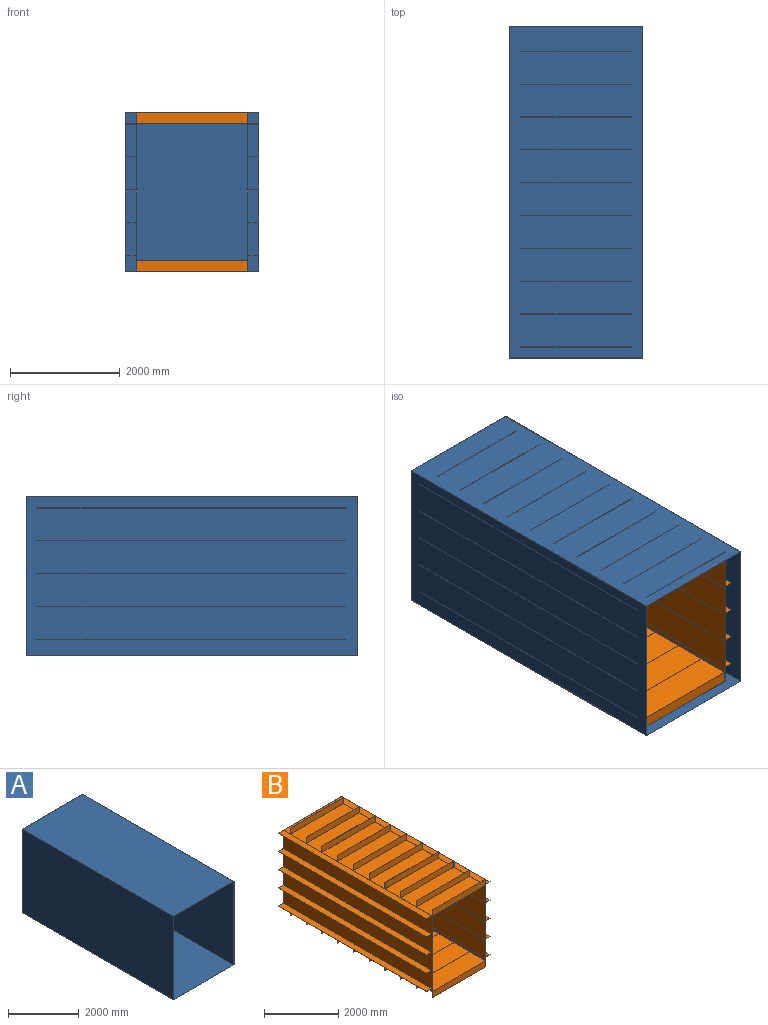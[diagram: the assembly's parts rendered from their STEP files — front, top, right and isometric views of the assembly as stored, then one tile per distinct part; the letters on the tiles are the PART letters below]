
ASSEMBLY  parts=2 mates=1
PART A: 11 faces, bbox 2438x6058x2896 mm
  f0: plane 6058x2438mm, normal (0,0,1), area 14769404mm2, adj f1,f7,f8,f9
  f1: plane 6058x2896mm, normal (-1,0,0), area 17543968mm2, adj f0,f2,f8,f9
  f2: plane 6058x2438mm, normal (0,0,-1), area 14769404mm2, adj f1,f7,f8,f9
  f3: plane 6055x2890mm, normal (1,0,0), area 17498950mm2, adj f4,f6,f8,f10
  f4: plane 6055x2432mm, normal (0,0,-1), area 14725760mm2, adj f3,f5,f8,f10
  f5: plane 6055x2890mm, normal (-1,0,0), area 17498950mm2, adj f4,f6,f8,f10
  f6: plane 6055x2432mm, normal (0,0,1), area 14725760mm2, adj f3,f5,f8,f10
  f7: plane 6058x2896mm, normal (1,0,0), area 17543968mm2, adj f0,f2,f8,f9
  f8: plane 2896x2438mm, normal (0,-1,0), area 31968mm2, adj f0,f1,f2,f3,f4,f5,f6,f7
  f9: plane 2896x2438mm, normal (0,1,0), area 7060448mm2, adj f0,f1,f2,f7
  f10: plane 2890x2432mm, normal (0,-1,0), area 7028480mm2, adj f3,f4,f5,f6
PART B: 135 faces, bbox 2432x5668x2890 mm
  f0: plane 5668x2032mm, normal (0,0,-1), area 11416076mm2, adj f2,f7,f8,f9,f97,f98,f99,f100
  f1: plane 5668x2432mm, normal (0,0,1), area 13671276mm2, adj f2,f7,f8,f9,f11,f12,f29,f31
  f2: plane 5668x2490mm, normal (-1,0,0), area 13972370mm2, adj f0,f1,f8,f9,f30,f31,f32,f34
  f3: plane 5668x2484mm, normal (1,0,0), area 14079312mm2, adj f4,f6,f8,f9
  f4: plane 5668x2026mm, normal (0,0,-1), area 11483368mm2, adj f3,f5,f8,f9
  f5: plane 5668x2484mm, normal (-1,0,0), area 14079312mm2, adj f4,f6,f8,f9
  f6: plane 5668x2026mm, normal (0,0,1), area 11483368mm2, adj f3,f5,f8,f9
  f7: plane 5668x2890mm, normal (1,0,0), area 13983370mm2, adj f0,f1,f8,f9,f10,f12,f13,f14
  f8: plane 2890x2032mm, normal (0,-1,0), area 837496mm2, adj f0,f1,f2,f3,f4,f5,f6,f7
  f9: plane 2490x2432mm, normal (0,1,0), area 37096mm2, adj f0,f1,f2,f3,f4,f5,f6,f7
  f10: plane 5638x200mm, normal (0,0,-1), area 1127600mm2, adj f7,f9,f11,f12
  f11: plane 5638x5mm, normal (1,0,0), area 28190mm2, adj f1,f9,f10,f12
  f12: plane 200x5mm, normal (0,-1,0), area 1000mm2, adj f1,f7,f10,f11
  f13: plane 5638x200mm, normal (0,0,1), area 1127600mm2, adj f7,f9,f15,f16
  f14: plane 5638x200mm, normal (0,0,-1), area 1127600mm2, adj f7,f9,f15,f16
  f15: plane 5638x5mm, normal (1,0,0), area 28190mm2, adj f9,f13,f14,f16
  f16: plane 200x5mm, normal (0,-1,0), area 1000mm2, adj f7,f13,f14,f15
  f17: plane 5638x200mm, normal (0,0,1), area 1127600mm2, adj f7,f9,f19,f20
  f18: plane 5638x200mm, normal (0,0,-1), area 1127600mm2, adj f7,f9,f19,f20
  f19: plane 5638x5mm, normal (1,0,0), area 28190mm2, adj f9,f17,f18,f20
  f20: plane 200x5mm, normal (0,-1,0), area 1000mm2, adj f7,f17,f18,f19
  f21: plane 5638x200mm, normal (0,0,1), area 1127600mm2, adj f7,f9,f23,f24
  f22: plane 5638x200mm, normal (0,0,-1), area 1127600mm2, adj f7,f9,f23,f24
  f23: plane 5638x5mm, normal (1,0,0), area 28190mm2, adj f9,f21,f22,f24
  f24: plane 200x5mm, normal (0,-1,0), area 1000mm2, adj f7,f21,f22,f23
  f25: plane 5638x200mm, normal (0,0,1), area 1127600mm2, adj f7,f9,f27,f28
  f26: plane 5638x200mm, normal (0,0,-1), area 1127600mm2, adj f7,f9,f27,f28
  f27: plane 5638x5mm, normal (1,0,0), area 28190mm2, adj f9,f25,f26,f28
  f28: plane 200x5mm, normal (0,-1,0), area 1000mm2, adj f7,f25,f26,f27
  f29: plane 5638x5mm, normal (-1,0,0), area 28190mm2, adj f1,f9,f30,f31
  f30: plane 5638x200mm, normal (0,0,-1), area 1127600mm2, adj f2,f9,f29,f31
  f31: plane 200x5mm, normal (0,-1,0), area 1000mm2, adj f1,f2,f29,f30
  f32: plane 5638x200mm, normal (0,0,1), area 1127600mm2, adj f2,f9,f33,f35
  f33: plane 5638x5mm, normal (-1,0,0), area 28190mm2, adj f9,f32,f34,f35
  f34: plane 5638x200mm, normal (0,0,-1), area 1127600mm2, adj f2,f9,f33,f35
  f35: plane 200x5mm, normal (0,-1,0), area 1000mm2, adj f2,f32,f33,f34
  f36: plane 5638x200mm, normal (0,0,1), area 1127600mm2, adj f2,f9,f37,f39
  f37: plane 5638x5mm, normal (-1,0,0), area 28190mm2, adj f9,f36,f38,f39
  f38: plane 5638x200mm, normal (0,0,-1), area 1127600mm2, adj f2,f9,f37,f39
  f39: plane 200x5mm, normal (0,-1,0), area 1000mm2, adj f2,f36,f37,f38
  f40: plane 5638x200mm, normal (0,0,1), area 1127600mm2, adj f2,f9,f41,f43
  f41: plane 5638x5mm, normal (-1,0,0), area 28190mm2, adj f9,f40,f42,f43
  f42: plane 5638x200mm, normal (0,0,-1), area 1127600mm2, adj f2,f9,f41,f43
  f43: plane 200x5mm, normal (0,-1,0), area 1000mm2, adj f2,f40,f41,f42
  f44: plane 5638x200mm, normal (0,0,1), area 1127600mm2, adj f2,f9,f45,f47
  f45: plane 5638x5mm, normal (-1,0,0), area 28190mm2, adj f9,f44,f46,f47
  f46: plane 5638x200mm, normal (0,0,-1), area 1127600mm2, adj f2,f9,f45,f47
  f47: plane 200x5mm, normal (0,-1,0), area 1000mm2, adj f2,f44,f45,f46
  f48: plane 2026x200mm, normal (0,1,0), area 405200mm2, adj f1,f7,f49,f50
  f49: plane 2026x5mm, normal (0,0,1), area 10130mm2, adj f7,f8,f48,f50
  f50: plane 200x5mm, normal (-1,0,0), area 1000mm2, adj f1,f8,f48,f49
  f51: plane 2026x200mm, normal (0,-1,0), area 405200mm2, adj f1,f53,f54,f55
  f52: plane 2026x200mm, normal (0,1,0), area 405200mm2, adj f1,f53,f54,f55
  f53: plane 2026x5mm, normal (0,0,1), area 10130mm2, adj f51,f52,f54,f55
  f54: plane 200x5mm, normal (-1,0,0), area 1000mm2, adj f1,f51,f52,f53
  f55: plane 200x5mm, normal (1,0,0), area 1000mm2, adj f1,f51,f52,f53
  f56: plane 2026x200mm, normal (0,-1,0), area 405200mm2, adj f1,f58,f59,f60
  f57: plane 2026x200mm, normal (0,1,0), area 405200mm2, adj f1,f58,f59,f60
  f58: plane 2026x5mm, normal (0,0,1), area 10130mm2, adj f56,f57,f59,f60
  f59: plane 200x5mm, normal (-1,0,0), area 1000mm2, adj f1,f56,f57,f58
  f60: plane 200x5mm, normal (1,0,0), area 1000mm2, adj f1,f56,f57,f58
  f61: plane 2026x200mm, normal (0,-1,0), area 405200mm2, adj f1,f63,f64,f65
  f62: plane 2026x200mm, normal (0,1,0), area 405200mm2, adj f1,f63,f64,f65
  f63: plane 2026x5mm, normal (0,0,1), area 10130mm2, adj f61,f62,f64,f65
  f64: plane 200x5mm, normal (-1,0,0), area 1000mm2, adj f1,f61,f62,f63
  f65: plane 200x5mm, normal (1,0,0), area 1000mm2, adj f1,f61,f62,f63
  f66: plane 2026x200mm, normal (0,-1,0), area 405200mm2, adj f1,f68,f69,f70
  f67: plane 2026x200mm, normal (0,1,0), area 405200mm2, adj f1,f68,f69,f70
  f68: plane 2026x5mm, normal (0,0,1), area 10130mm2, adj f66,f67,f69,f70
  f69: plane 200x5mm, normal (-1,0,0), area 1000mm2, adj f1,f66,f67,f68
  f70: plane 200x5mm, normal (1,0,0), area 1000mm2, adj f1,f66,f67,f68
  f71: plane 2026x200mm, normal (0,-1,0), area 405200mm2, adj f1,f73,f74,f75
  f72: plane 2026x200mm, normal (0,1,0), area 405200mm2, adj f1,f73,f74,f75
  f73: plane 2026x5mm, normal (0,0,1), area 10130mm2, adj f71,f72,f74,f75
  f74: plane 200x5mm, normal (-1,0,0), area 1000mm2, adj f1,f71,f72,f73
  f75: plane 200x5mm, normal (1,0,0), area 1000mm2, adj f1,f71,f72,f73
  f76: plane 2026x200mm, normal (0,-1,0), area 405200mm2, adj f1,f78,f79,f80
  f77: plane 2026x200mm, normal (0,1,0), area 405200mm2, adj f1,f78,f79,f80
  f78: plane 2026x5mm, normal (0,0,1), area 10130mm2, adj f76,f77,f79,f80
  f79: plane 200x5mm, normal (-1,0,0), area 1000mm2, adj f1,f76,f77,f78
  f80: plane 200x5mm, normal (1,0,0), area 1000mm2, adj f1,f76,f77,f78
  f81: plane 2026x200mm, normal (0,-1,0), area 405200mm2, adj f1,f83,f84,f85
  f82: plane 2026x200mm, normal (0,1,0), area 405200mm2, adj f1,f83,f84,f85
  f83: plane 2026x5mm, normal (0,0,1), area 10130mm2, adj f81,f82,f84,f85
  f84: plane 200x5mm, normal (-1,0,0), area 1000mm2, adj f1,f81,f82,f83
  f85: plane 200x5mm, normal (1,0,0), area 1000mm2, adj f1,f81,f82,f83
  f86: plane 2026x200mm, normal (0,-1,0), area 405200mm2, adj f1,f88,f89,f90
  f87: plane 2026x200mm, normal (0,1,0), area 405200mm2, adj f1,f88,f89,f90
  f88: plane 2026x5mm, normal (0,0,1), area 10130mm2, adj f86,f87,f89,f90
  f89: plane 200x5mm, normal (-1,0,0), area 1000mm2, adj f1,f86,f87,f88
  f90: plane 200x5mm, normal (1,0,0), area 1000mm2, adj f1,f86,f87,f88
  f91: plane 2026x200mm, normal (0,-1,0), area 405200mm2, adj f1,f93,f94,f95
  f92: plane 2026x200mm, normal (0,1,0), area 405200mm2, adj f1,f93,f94,f95
  f93: plane 2026x5mm, normal (0,0,1), area 10130mm2, adj f91,f92,f94,f95
  f94: plane 200x5mm, normal (-1,0,0), area 1000mm2, adj f1,f91,f92,f93
  f95: plane 200x5mm, normal (1,0,0), area 1000mm2, adj f1,f91,f92,f93
  f96: plane 2026x5mm, normal (0,0,-1), area 10130mm2, adj f7,f8,f97,f98
  f97: plane 2026x200mm, normal (0,1,0), area 405200mm2, adj f0,f7,f96,f98
  f98: plane 200x5mm, normal (-1,0,0), area 1000mm2, adj f0,f8,f96,f97
  f99: plane 2026x200mm, normal (0,1,0), area 405200mm2, adj f0,f7,f101,f102
  f100: plane 2026x200mm, normal (0,-1,0), area 405200mm2, adj f0,f7,f101,f102
  f101: plane 2026x5mm, normal (0,0,-1), area 10130mm2, adj f7,f99,f100,f102
  f102: plane 200x5mm, normal (-1,0,0), area 1000mm2, adj f0,f99,f100,f101
  f103: plane 2026x200mm, normal (0,1,0), area 405200mm2, adj f0,f7,f105,f106
  f104: plane 2026x200mm, normal (0,-1,0), area 405200mm2, adj f0,f7,f105,f106
  f105: plane 2026x5mm, normal (0,0,-1), area 10130mm2, adj f7,f103,f104,f106
  f106: plane 200x5mm, normal (-1,0,0), area 1000mm2, adj f0,f103,f104,f105
  f107: plane 2026x200mm, normal (0,1,0), area 405200mm2, adj f0,f7,f109,f110
  f108: plane 2026x200mm, normal (0,-1,0), area 405200mm2, adj f0,f7,f109,f110
  f109: plane 2026x5mm, normal (0,0,-1), area 10130mm2, adj f7,f107,f108,f110
  f110: plane 200x5mm, normal (-1,0,0), area 1000mm2, adj f0,f107,f108,f109
  f111: plane 2026x200mm, normal (0,1,0), area 405200mm2, adj f0,f7,f113,f114
  f112: plane 2026x200mm, normal (0,-1,0), area 405200mm2, adj f0,f7,f113,f114
  f113: plane 2026x5mm, normal (0,0,-1), area 10130mm2, adj f7,f111,f112,f114
  f114: plane 200x5mm, normal (-1,0,0), area 1000mm2, adj f0,f111,f112,f113
  f115: plane 2026x200mm, normal (0,1,0), area 405200mm2, adj f0,f7,f117,f118
  f116: plane 2026x200mm, normal (0,-1,0), area 405200mm2, adj f0,f7,f117,f118
  f117: plane 2026x5mm, normal (0,0,-1), area 10130mm2, adj f7,f115,f116,f118
  f118: plane 200x5mm, normal (-1,0,0), area 1000mm2, adj f0,f115,f116,f117
  f119: plane 2026x200mm, normal (0,1,0), area 405200mm2, adj f0,f7,f121,f122
  f120: plane 2026x200mm, normal (0,-1,0), area 405200mm2, adj f0,f7,f121,f122
  f121: plane 2026x5mm, normal (0,0,-1), area 10130mm2, adj f7,f119,f120,f122
  f122: plane 200x5mm, normal (-1,0,0), area 1000mm2, adj f0,f119,f120,f121
  f123: plane 2026x200mm, normal (0,1,0), area 405200mm2, adj f0,f7,f125,f126
  f124: plane 2026x200mm, normal (0,-1,0), area 405200mm2, adj f0,f7,f125,f126
  f125: plane 2026x5mm, normal (0,0,-1), area 10130mm2, adj f7,f123,f124,f126
  f126: plane 200x5mm, normal (-1,0,0), area 1000mm2, adj f0,f123,f124,f125
  f127: plane 2026x200mm, normal (0,1,0), area 405200mm2, adj f0,f7,f129,f130
  f128: plane 2026x200mm, normal (0,-1,0), area 405200mm2, adj f0,f7,f129,f130
  f129: plane 2026x5mm, normal (0,0,-1), area 10130mm2, adj f7,f127,f128,f130
  f130: plane 200x5mm, normal (-1,0,0), area 1000mm2, adj f0,f127,f128,f129
  f131: plane 2026x200mm, normal (0,1,0), area 405200mm2, adj f0,f7,f133,f134
  f132: plane 2026x200mm, normal (0,-1,0), area 405200mm2, adj f0,f7,f133,f134
  f133: plane 2026x5mm, normal (0,0,-1), area 10130mm2, adj f7,f131,f132,f134
  f134: plane 200x5mm, normal (-1,0,0), area 1000mm2, adj f0,f131,f132,f133
PLACE A t=(-1749.14,1148.05,-1509.63)mm
PLACE B t=(-1749.14,951.55,-1509.63)mm
MATE parallel B.f6 <-> A.f6  axis (0,0,1) through (-1749.14,-1882.45,-2751.63)mm
